annotation { "Feature Type Name" : "Feature", "Feature Type Description" : "" }
export const myFeature = defineFeature(function(context is Context, id is Id, definition is map)
    precondition{}
    {
        {
            assignVariable(context, id + "F0", {"name" : "Offset", "anyValue" : .2});
        }
        {
            assignVariable(context, id + "F1", {"name" : "WallThick", "anyValue" : 1.2});
        }
        {
            assignVariable(context, id + "F2", {"name" : "TileThick3", "anyValue" : 6});
        }
        {
            assignVariable(context, id + "F3", {"name" : "TileThick4", "anyValue" : 8});
        }
        {
            assignVariable(context, id + "F4", {"name" : "TileSide", "anyValue" : 20.2});
        }
        {
            var Q0;
            Q0=qCreatedBy(makeId("Front.planeOp"),FACE);
            var sketch = newSketch(context, id + "F5", { "sketchPlane" : qUnion([Q0])});
            skLineSegment(sketch, "E0.bottom", {"start": v(10.1, -10.1) * mm, "end": v(-10.1, -10.1) * mm});
            skLineSegment(sketch, "E0.top", {"start": v(10.1, 10.1) * mm, "end": v(-10.1, 10.1) * mm});
            skLineSegment(sketch, "E0.left", {"start": v(10.1, -10.1) * mm, "end": v(10.1, 10.1) * mm});
            skLineSegment(sketch, "E0.right", {"start": v(-10.1, -10.1) * mm, "end": v(-10.1, 10.1) * mm});
            skPoint(sketch, "E0.middle", {"position": v(0, 0) * mm});
            skSolve(sketch);
        }
        {
            var Q0;
            Q0 = qSketchRegion(id + "F5", true);
            extrude(context, id + "F6", {"entities" : qUnion([Q0]), "oppositeDirection" : true, "depth" : (getVariable(context, 'TileThick3')) * mm, "offsetDistance" : 25 * mm});
        }
        {
            var Q0;
            Q0=makeQuery(id+"F6.opExtrude","SWEPT_EDGE",EDGE,{"disambiguationData":[OSD([sQuery(id+"F5.wireOp",EDGE,"E0.top"),sQuery(id+"F5.wireOp",EDGE,"E0.left")])]});
            var Q1;
            Q1=makeQuery(id+"F6.opExtrude","SWEPT_EDGE",EDGE,{"disambiguationData":[OSD([sQuery(id+"F5.wireOp",EDGE,"E0.top"),sQuery(id+"F5.wireOp",EDGE,"E0.right")])]});
            var Q2;
            Q2=makeQuery(id+"F6.opExtrude","SWEPT_EDGE",EDGE,{"disambiguationData":[OSD([sQuery(id+"F5.wireOp",EDGE,"E0.bottom"),sQuery(id+"F5.wireOp",EDGE,"E0.right")])]});
            var Q3;
            Q3=makeQuery(id+"F6.opExtrude","SWEPT_EDGE",EDGE,{"disambiguationData":[OSD([sQuery(id+"F5.wireOp",EDGE,"E0.bottom"),sQuery(id+"F5.wireOp",EDGE,"E0.left")])]});
            fillet(context, id + "F7", {"entities" : qUnion([Q0, Q1, Q2, Q3]), "radius" : 1.5 * mm, "tangentPropagation" : true, "allowEdgeOverflow" : false});
        }
        {
            var Q0;
            Q0=makeQuery(id+"F6.opExtrude","SWEPT_FACE",FACE,{"disambiguationData":[OSD([sQuery(id+"F5.wireOp",EDGE,"E0.bottom")])]});
            cPlane(context, id + "F8", {"entities" : qUnion([Q0]), "cplaneType" : CPlaneType.OFFSET, "offset" : (getVariable(context, 'TileSide') - 8) * mm, "oppositeDirection" : true, "width" : 150 * mm, "height" : 150 * mm});
        }
        {
            var Q0;
            Q0=qCreatedBy(id+"F8.planeOp",FACE);
            var sketch = newSketch(context, id + "F9", { "sketchPlane" : qUnion([Q0])});
            skLineSegment(sketch, "E1.0", {"start": v(15, 0.2) * mm, "end": v(10.3, 0.2) * mm});
            skLineSegment(sketch, "E1.1", {"start": v(10.3, -6.2) * mm, "end": v(10.3, 0.2) * mm});
            skLineSegment(sketch, "E1.2", {"start": v(15, 0.2) * mm, "end": v(-2.2, 0.2) * mm});
            skLineSegment(sketch, "E1.3", {"start": v(10.3, -6.2) * mm, "end": v(15, -6.2) * mm});
            skLineSegment(sketch, "E1.4", {"start": v(-2.2, 0.2) * mm, "end": v(-10.3, 0.2) * mm});
            skLineSegment(sketch, "E1.5", {"start": v(-10.3, 0.2) * mm, "end": v(-10.3, -6.2) * mm});
            skLineSegment(sketch, "E1.6", {"start": v(-10.3, -6.2) * mm, "end": v(-2.2, -6.2) * mm});
            skLineSegment(sketch, "E1.7", {"start": v(15, -6.2) * mm, "end": v(-2.2, -6.2) * mm});
            skLineSegment(sketch, "E2.0", {"start": v(11.5, -7.4) * mm, "end": v(11.8, -7.4) * mm});
            skLineSegment(sketch, "E2.1", {"start": v(11.5, -7.4) * mm, "end": v(11.5, 1.4) * mm});
            skLineSegment(sketch, "E2.2", {"start": v(11.8, -7.4) * mm, "end": v(-2.2, -7.4) * mm});
            skLineSegment(sketch, "E2.3", {"start": v(15, 1.4) * mm, "end": v(11.5, 1.4) * mm});
            skLineSegment(sketch, "E2.4", {"start": v(-11.5, -7.4) * mm, "end": v(-2.2, -7.4) * mm});
            skLineSegment(sketch, "E2.5", {"start": v(-11.5, 1.4) * mm, "end": v(-11.5, -7.4) * mm});
            skLineSegment(sketch, "E2.6", {"start": v(-5.4, 1.4) * mm, "end": v(-11.5, 1.4) * mm});
            skLineSegment(sketch, "E2.7", {"start": v(15, 1.4) * mm, "end": v(-5.4, 1.4) * mm});
            skLineSegment(sketch, "E3.0.1.0", {"start": v(-11.5, -15) * mm, "end": v(-2.2, -15) * mm});
            skLineSegment(sketch, "E3.0.1.1", {"start": v(15, -6.2) * mm, "end": v(11.5, -6.2) * mm});
            skLineSegment(sketch, "E3.0.1.2", {"start": v(11.8, -15) * mm, "end": v(-2.2, -15) * mm});
            skLineSegment(sketch, "E3.0.1.3", {"start": v(11.5, -15) * mm, "end": v(11.5, -6.2) * mm});
            skLineSegment(sketch, "E3.0.1.4", {"start": v(11.5, -15) * mm, "end": v(11.8, -15) * mm});
            skLineSegment(sketch, "E3.0.1.5", {"start": v(15, -13.8) * mm, "end": v(-2.2, -13.8) * mm});
            skLineSegment(sketch, "E3.0.1.6", {"start": v(-10.3, -7.4) * mm, "end": v(-10.3, -13.8) * mm});
            skLineSegment(sketch, "E3.0.1.7", {"start": v(15, -7.4) * mm, "end": v(-2.2, -7.4) * mm});
            skLineSegment(sketch, "E3.0.1.8", {"start": v(10.3, -13.8) * mm, "end": v(10.3, -7.4) * mm});
            skLineSegment(sketch, "E3.0.1.9", {"start": v(15, -6.2) * mm, "end": v(-5.4, -6.2) * mm});
            skLineSegment(sketch, "E3.0.1.10", {"start": v(-5.4, -6.2) * mm, "end": v(-11.5, -6.2) * mm});
            skLineSegment(sketch, "E3.0.1.11", {"start": v(-11.5, -6.2) * mm, "end": v(-11.5, -15) * mm});
            skLineSegment(sketch, "E3.0.1.12", {"start": v(-10.3, -13.8) * mm, "end": v(-2.2, -13.8) * mm});
            skLineSegment(sketch, "E3.0.1.13", {"start": v(-2.2, -7.4) * mm, "end": v(-10.3, -7.4) * mm});
            skLineSegment(sketch, "E3.0.1.14", {"start": v(10.3, -13.8) * mm, "end": v(15, -13.8) * mm});
            skLineSegment(sketch, "E3.0.1.15", {"start": v(15, -7.4) * mm, "end": v(10.3, -7.4) * mm});
            skLineSegment(sketch, "E3.0.2.0", {"start": v(-11.5, -22.6) * mm, "end": v(-2.2, -22.6) * mm});
            skLineSegment(sketch, "E3.0.2.1", {"start": v(15, -13.8) * mm, "end": v(11.5, -13.8) * mm});
            skLineSegment(sketch, "E3.0.2.2", {"start": v(11.8, -22.6) * mm, "end": v(-2.2, -22.6) * mm});
            skLineSegment(sketch, "E3.0.2.3", {"start": v(11.5, -22.6) * mm, "end": v(11.5, -13.8) * mm});
            skLineSegment(sketch, "E3.0.2.4", {"start": v(11.5, -22.6) * mm, "end": v(11.8, -22.6) * mm});
            skLineSegment(sketch, "E3.0.2.5", {"start": v(15, -21.4) * mm, "end": v(-2.2, -21.4) * mm});
            skLineSegment(sketch, "E3.0.2.6", {"start": v(-10.3, -15) * mm, "end": v(-10.3, -21.4) * mm});
            skLineSegment(sketch, "E3.0.2.7", {"start": v(15, -15) * mm, "end": v(-2.2, -15) * mm});
            skLineSegment(sketch, "E3.0.2.8", {"start": v(10.3, -21.4) * mm, "end": v(10.3, -15) * mm});
            skLineSegment(sketch, "E3.0.2.9", {"start": v(15, -13.8) * mm, "end": v(-5.4, -13.8) * mm});
            skLineSegment(sketch, "E3.0.2.10", {"start": v(-5.4, -13.8) * mm, "end": v(-11.5, -13.8) * mm});
            skLineSegment(sketch, "E3.0.2.11", {"start": v(-11.5, -13.8) * mm, "end": v(-11.5, -22.6) * mm});
            skLineSegment(sketch, "E3.0.2.12", {"start": v(-10.3, -21.4) * mm, "end": v(-2.2, -21.4) * mm});
            skLineSegment(sketch, "E3.0.2.13", {"start": v(-2.2, -15) * mm, "end": v(-10.3, -15) * mm});
            skLineSegment(sketch, "E3.0.2.14", {"start": v(10.3, -21.4) * mm, "end": v(15, -21.4) * mm});
            skLineSegment(sketch, "E3.0.2.15", {"start": v(15, -15) * mm, "end": v(10.3, -15) * mm});
            skLineSegment(sketch, "E3.0.3.0", {"start": v(-11.5, -30.2) * mm, "end": v(-2.2, -30.2) * mm});
            skLineSegment(sketch, "E3.0.3.1", {"start": v(15, -21.4) * mm, "end": v(11.5, -21.4) * mm});
            skLineSegment(sketch, "E3.0.3.2", {"start": v(11.8, -30.2) * mm, "end": v(-2.2, -30.2) * mm});
            skLineSegment(sketch, "E3.0.3.3", {"start": v(11.5, -30.2) * mm, "end": v(11.5, -21.4) * mm});
            skLineSegment(sketch, "E3.0.3.4", {"start": v(11.5, -30.2) * mm, "end": v(11.8, -30.2) * mm});
            skLineSegment(sketch, "E3.0.3.5", {"start": v(15, -29) * mm, "end": v(-2.2, -29) * mm});
            skLineSegment(sketch, "E3.0.3.6", {"start": v(-10.3, -22.6) * mm, "end": v(-10.3, -29) * mm});
            skLineSegment(sketch, "E3.0.3.7", {"start": v(15, -22.6) * mm, "end": v(-2.2, -22.6) * mm});
            skLineSegment(sketch, "E3.0.3.8", {"start": v(10.3, -29) * mm, "end": v(10.3, -22.6) * mm});
            skLineSegment(sketch, "E3.0.3.9", {"start": v(15, -21.4) * mm, "end": v(-5.4, -21.4) * mm});
            skLineSegment(sketch, "E3.0.3.10", {"start": v(-5.4, -21.4) * mm, "end": v(-11.5, -21.4) * mm});
            skLineSegment(sketch, "E3.0.3.11", {"start": v(-11.5, -21.4) * mm, "end": v(-11.5, -30.2) * mm});
            skLineSegment(sketch, "E3.0.3.12", {"start": v(-10.3, -29) * mm, "end": v(-2.2, -29) * mm});
            skLineSegment(sketch, "E3.0.3.13", {"start": v(-2.2, -22.6) * mm, "end": v(-10.3, -22.6) * mm});
            skLineSegment(sketch, "E3.0.3.14", {"start": v(10.3, -29) * mm, "end": v(15, -29) * mm});
            skLineSegment(sketch, "E3.0.3.15", {"start": v(15, -22.6) * mm, "end": v(10.3, -22.6) * mm});
            skLineSegment(sketch, "E3.1.0.0", {"start": v(10.3, -7.4) * mm, "end": v(19.6, -7.4) * mm});
            skLineSegment(sketch, "E3.1.0.1", {"start": v(36.8, 1.4) * mm, "end": v(33.3, 1.4) * mm});
            skLineSegment(sketch, "E3.1.0.2", {"start": v(33.6, -7.4) * mm, "end": v(19.6, -7.4) * mm});
            skLineSegment(sketch, "E3.1.0.3", {"start": v(33.3, -7.4) * mm, "end": v(33.3, 1.4) * mm});
            skLineSegment(sketch, "E3.1.0.4", {"start": v(33.3, -7.4) * mm, "end": v(33.6, -7.4) * mm});
            skLineSegment(sketch, "E3.1.0.5", {"start": v(36.8, -6.2) * mm, "end": v(19.6, -6.2) * mm});
            skLineSegment(sketch, "E3.1.0.6", {"start": v(11.5, 0.2) * mm, "end": v(11.5, -6.2) * mm});
            skLineSegment(sketch, "E3.1.0.7", {"start": v(36.8, 0.2) * mm, "end": v(19.6, 0.2) * mm});
            skLineSegment(sketch, "E3.1.0.8", {"start": v(32.1, -6.2) * mm, "end": v(32.1, 0.2) * mm});
            skLineSegment(sketch, "E3.1.0.9", {"start": v(36.8, 1.4) * mm, "end": v(16.4, 1.4) * mm});
            skLineSegment(sketch, "E3.1.0.10", {"start": v(16.4, 1.4) * mm, "end": v(10.3, 1.4) * mm});
            skLineSegment(sketch, "E3.1.0.11", {"start": v(10.3, 1.4) * mm, "end": v(10.3, -7.4) * mm});
            skLineSegment(sketch, "E3.1.0.12", {"start": v(11.5, -6.2) * mm, "end": v(19.6, -6.2) * mm});
            skLineSegment(sketch, "E3.1.0.13", {"start": v(19.6, 0.2) * mm, "end": v(11.5, 0.2) * mm});
            skLineSegment(sketch, "E3.1.0.14", {"start": v(32.1, -6.2) * mm, "end": v(36.8, -6.2) * mm});
            skLineSegment(sketch, "E3.1.0.15", {"start": v(36.8, 0.2) * mm, "end": v(32.1, 0.2) * mm});
            skLineSegment(sketch, "E3.1.1.0", {"start": v(10.3, -15) * mm, "end": v(19.6, -15) * mm});
            skLineSegment(sketch, "E3.1.1.1", {"start": v(36.8, -6.2) * mm, "end": v(33.3, -6.2) * mm});
            skLineSegment(sketch, "E3.1.1.2", {"start": v(33.6, -15) * mm, "end": v(19.6, -15) * mm});
            skLineSegment(sketch, "E3.1.1.3", {"start": v(33.3, -15) * mm, "end": v(33.3, -6.2) * mm});
            skLineSegment(sketch, "E3.1.1.4", {"start": v(33.3, -15) * mm, "end": v(33.6, -15) * mm});
            skLineSegment(sketch, "E3.1.1.5", {"start": v(36.8, -13.8) * mm, "end": v(19.6, -13.8) * mm});
            skLineSegment(sketch, "E3.1.1.6", {"start": v(11.5, -7.4) * mm, "end": v(11.5, -13.8) * mm});
            skLineSegment(sketch, "E3.1.1.7", {"start": v(36.8, -7.4) * mm, "end": v(19.6, -7.4) * mm});
            skLineSegment(sketch, "E3.1.1.8", {"start": v(32.1, -13.8) * mm, "end": v(32.1, -7.4) * mm});
            skLineSegment(sketch, "E3.1.1.9", {"start": v(36.8, -6.2) * mm, "end": v(16.4, -6.2) * mm});
            skLineSegment(sketch, "E3.1.1.10", {"start": v(16.4, -6.2) * mm, "end": v(10.3, -6.2) * mm});
            skLineSegment(sketch, "E3.1.1.11", {"start": v(10.3, -6.2) * mm, "end": v(10.3, -15) * mm});
            skLineSegment(sketch, "E3.1.1.12", {"start": v(11.5, -13.8) * mm, "end": v(19.6, -13.8) * mm});
            skLineSegment(sketch, "E3.1.1.13", {"start": v(19.6, -7.4) * mm, "end": v(11.5, -7.4) * mm});
            skLineSegment(sketch, "E3.1.1.14", {"start": v(32.1, -13.8) * mm, "end": v(36.8, -13.8) * mm});
            skLineSegment(sketch, "E3.1.1.15", {"start": v(36.8, -7.4) * mm, "end": v(32.1, -7.4) * mm});
            skLineSegment(sketch, "E3.1.2.0", {"start": v(10.3, -22.6) * mm, "end": v(19.6, -22.6) * mm});
            skLineSegment(sketch, "E3.1.2.1", {"start": v(36.8, -13.8) * mm, "end": v(33.3, -13.8) * mm});
            skLineSegment(sketch, "E3.1.2.2", {"start": v(33.6, -22.6) * mm, "end": v(19.6, -22.6) * mm});
            skLineSegment(sketch, "E3.1.2.3", {"start": v(33.3, -22.6) * mm, "end": v(33.3, -13.8) * mm});
            skLineSegment(sketch, "E3.1.2.4", {"start": v(33.3, -22.6) * mm, "end": v(33.6, -22.6) * mm});
            skLineSegment(sketch, "E3.1.2.5", {"start": v(36.8, -21.4) * mm, "end": v(19.6, -21.4) * mm});
            skLineSegment(sketch, "E3.1.2.6", {"start": v(11.5, -15) * mm, "end": v(11.5, -21.4) * mm});
            skLineSegment(sketch, "E3.1.2.7", {"start": v(36.8, -15) * mm, "end": v(19.6, -15) * mm});
            skLineSegment(sketch, "E3.1.2.8", {"start": v(32.1, -21.4) * mm, "end": v(32.1, -15) * mm});
            skLineSegment(sketch, "E3.1.2.9", {"start": v(36.8, -13.8) * mm, "end": v(16.4, -13.8) * mm});
            skLineSegment(sketch, "E3.1.2.10", {"start": v(16.4, -13.8) * mm, "end": v(10.3, -13.8) * mm});
            skLineSegment(sketch, "E3.1.2.11", {"start": v(10.3, -13.8) * mm, "end": v(10.3, -22.6) * mm});
            skLineSegment(sketch, "E3.1.2.12", {"start": v(11.5, -21.4) * mm, "end": v(19.6, -21.4) * mm});
            skLineSegment(sketch, "E3.1.2.13", {"start": v(19.6, -15) * mm, "end": v(11.5, -15) * mm});
            skLineSegment(sketch, "E3.1.2.14", {"start": v(32.1, -21.4) * mm, "end": v(36.8, -21.4) * mm});
            skLineSegment(sketch, "E3.1.2.15", {"start": v(36.8, -15) * mm, "end": v(32.1, -15) * mm});
            skLineSegment(sketch, "E3.1.3.0", {"start": v(10.3, -30.2) * mm, "end": v(19.6, -30.2) * mm});
            skLineSegment(sketch, "E3.1.3.1", {"start": v(36.8, -21.4) * mm, "end": v(33.3, -21.4) * mm});
            skLineSegment(sketch, "E3.1.3.2", {"start": v(33.6, -30.2) * mm, "end": v(19.6, -30.2) * mm});
            skLineSegment(sketch, "E3.1.3.3", {"start": v(33.3, -30.2) * mm, "end": v(33.3, -21.4) * mm});
            skLineSegment(sketch, "E3.1.3.4", {"start": v(33.3, -30.2) * mm, "end": v(33.6, -30.2) * mm});
            skLineSegment(sketch, "E3.1.3.5", {"start": v(36.8, -29) * mm, "end": v(19.6, -29) * mm});
            skLineSegment(sketch, "E3.1.3.6", {"start": v(11.5, -22.6) * mm, "end": v(11.5, -29) * mm});
            skLineSegment(sketch, "E3.1.3.7", {"start": v(36.8, -22.6) * mm, "end": v(19.6, -22.6) * mm});
            skLineSegment(sketch, "E3.1.3.8", {"start": v(32.1, -29) * mm, "end": v(32.1, -22.6) * mm});
            skLineSegment(sketch, "E3.1.3.9", {"start": v(36.8, -21.4) * mm, "end": v(16.4, -21.4) * mm});
            skLineSegment(sketch, "E3.1.3.10", {"start": v(16.4, -21.4) * mm, "end": v(10.3, -21.4) * mm});
            skLineSegment(sketch, "E3.1.3.11", {"start": v(10.3, -21.4) * mm, "end": v(10.3, -30.2) * mm});
            skLineSegment(sketch, "E3.1.3.12", {"start": v(11.5, -29) * mm, "end": v(19.6, -29) * mm});
            skLineSegment(sketch, "E3.1.3.13", {"start": v(19.6, -22.6) * mm, "end": v(11.5, -22.6) * mm});
            skLineSegment(sketch, "E3.1.3.14", {"start": v(32.1, -29) * mm, "end": v(36.8, -29) * mm});
            skLineSegment(sketch, "E3.1.3.15", {"start": v(36.8, -22.6) * mm, "end": v(32.1, -22.6) * mm});
            skLineSegment(sketch, "E3.2.0.0", {"start": v(32.1, -7.4) * mm, "end": v(41.4, -7.4) * mm});
            skLineSegment(sketch, "E3.2.0.1", {"start": v(58.6, 1.4) * mm, "end": v(55.1, 1.4) * mm});
            skLineSegment(sketch, "E3.2.0.2", {"start": v(55.4, -7.4) * mm, "end": v(41.4, -7.4) * mm});
            skLineSegment(sketch, "E3.2.0.3", {"start": v(55.1, -7.4) * mm, "end": v(55.1, 1.4) * mm});
            skLineSegment(sketch, "E3.2.0.4", {"start": v(55.1, -7.4) * mm, "end": v(55.4, -7.4) * mm});
            skLineSegment(sketch, "E3.2.0.5", {"start": v(58.6, -6.2) * mm, "end": v(41.4, -6.2) * mm});
            skLineSegment(sketch, "E3.2.0.6", {"start": v(33.3, 0.2) * mm, "end": v(33.3, -6.2) * mm});
            skLineSegment(sketch, "E3.2.0.7", {"start": v(58.6, 0.2) * mm, "end": v(41.4, 0.2) * mm});
            skLineSegment(sketch, "E3.2.0.8", {"start": v(53.9, -6.2) * mm, "end": v(53.9, 0.2) * mm});
            skLineSegment(sketch, "E3.2.0.9", {"start": v(58.6, 1.4) * mm, "end": v(38.2, 1.4) * mm});
            skLineSegment(sketch, "E3.2.0.10", {"start": v(38.2, 1.4) * mm, "end": v(32.1, 1.4) * mm});
            skLineSegment(sketch, "E3.2.0.11", {"start": v(32.1, 1.4) * mm, "end": v(32.1, -7.4) * mm});
            skLineSegment(sketch, "E3.2.0.12", {"start": v(33.3, -6.2) * mm, "end": v(41.4, -6.2) * mm});
            skLineSegment(sketch, "E3.2.0.13", {"start": v(41.4, 0.2) * mm, "end": v(33.3, 0.2) * mm});
            skLineSegment(sketch, "E3.2.0.14", {"start": v(53.9, -6.2) * mm, "end": v(58.6, -6.2) * mm});
            skLineSegment(sketch, "E3.2.0.15", {"start": v(58.6, 0.2) * mm, "end": v(53.9, 0.2) * mm});
            skLineSegment(sketch, "E3.2.1.0", {"start": v(32.1, -15) * mm, "end": v(41.4, -15) * mm});
            skLineSegment(sketch, "E3.2.1.1", {"start": v(58.6, -6.2) * mm, "end": v(55.1, -6.2) * mm});
            skLineSegment(sketch, "E3.2.1.2", {"start": v(55.4, -15) * mm, "end": v(41.4, -15) * mm});
            skLineSegment(sketch, "E3.2.1.3", {"start": v(55.1, -15) * mm, "end": v(55.1, -6.2) * mm});
            skLineSegment(sketch, "E3.2.1.4", {"start": v(55.1, -15) * mm, "end": v(55.4, -15) * mm});
            skLineSegment(sketch, "E3.2.1.5", {"start": v(58.6, -13.8) * mm, "end": v(41.4, -13.8) * mm});
            skLineSegment(sketch, "E3.2.1.6", {"start": v(33.3, -7.4) * mm, "end": v(33.3, -13.8) * mm});
            skLineSegment(sketch, "E3.2.1.7", {"start": v(58.6, -7.4) * mm, "end": v(41.4, -7.4) * mm});
            skLineSegment(sketch, "E3.2.1.8", {"start": v(53.9, -13.8) * mm, "end": v(53.9, -7.4) * mm});
            skLineSegment(sketch, "E3.2.1.9", {"start": v(58.6, -6.2) * mm, "end": v(38.2, -6.2) * mm});
            skLineSegment(sketch, "E3.2.1.10", {"start": v(38.2, -6.2) * mm, "end": v(32.1, -6.2) * mm});
            skLineSegment(sketch, "E3.2.1.11", {"start": v(32.1, -6.2) * mm, "end": v(32.1, -15) * mm});
            skLineSegment(sketch, "E3.2.1.12", {"start": v(33.3, -13.8) * mm, "end": v(41.4, -13.8) * mm});
            skLineSegment(sketch, "E3.2.1.13", {"start": v(41.4, -7.4) * mm, "end": v(33.3, -7.4) * mm});
            skLineSegment(sketch, "E3.2.1.14", {"start": v(53.9, -13.8) * mm, "end": v(58.6, -13.8) * mm});
            skLineSegment(sketch, "E3.2.1.15", {"start": v(58.6, -7.4) * mm, "end": v(53.9, -7.4) * mm});
            skLineSegment(sketch, "E3.2.2.0", {"start": v(32.1, -22.6) * mm, "end": v(41.4, -22.6) * mm});
            skLineSegment(sketch, "E3.2.2.1", {"start": v(58.6, -13.8) * mm, "end": v(55.1, -13.8) * mm});
            skLineSegment(sketch, "E3.2.2.2", {"start": v(55.4, -22.6) * mm, "end": v(41.4, -22.6) * mm});
            skLineSegment(sketch, "E3.2.2.3", {"start": v(55.1, -22.6) * mm, "end": v(55.1, -13.8) * mm});
            skLineSegment(sketch, "E3.2.2.4", {"start": v(55.1, -22.6) * mm, "end": v(55.4, -22.6) * mm});
            skLineSegment(sketch, "E3.2.2.5", {"start": v(58.6, -21.4) * mm, "end": v(41.4, -21.4) * mm});
            skLineSegment(sketch, "E3.2.2.6", {"start": v(33.3, -15) * mm, "end": v(33.3, -21.4) * mm});
            skLineSegment(sketch, "E3.2.2.7", {"start": v(58.6, -15) * mm, "end": v(41.4, -15) * mm});
            skLineSegment(sketch, "E3.2.2.8", {"start": v(53.9, -21.4) * mm, "end": v(53.9, -15) * mm});
            skLineSegment(sketch, "E3.2.2.9", {"start": v(58.6, -13.8) * mm, "end": v(38.2, -13.8) * mm});
            skLineSegment(sketch, "E3.2.2.10", {"start": v(38.2, -13.8) * mm, "end": v(32.1, -13.8) * mm});
            skLineSegment(sketch, "E3.2.2.11", {"start": v(32.1, -13.8) * mm, "end": v(32.1, -22.6) * mm});
            skLineSegment(sketch, "E3.2.2.12", {"start": v(33.3, -21.4) * mm, "end": v(41.4, -21.4) * mm});
            skLineSegment(sketch, "E3.2.2.13", {"start": v(41.4, -15) * mm, "end": v(33.3, -15) * mm});
            skLineSegment(sketch, "E3.2.2.14", {"start": v(53.9, -21.4) * mm, "end": v(58.6, -21.4) * mm});
            skLineSegment(sketch, "E3.2.2.15", {"start": v(58.6, -15) * mm, "end": v(53.9, -15) * mm});
            skLineSegment(sketch, "E3.2.3.0", {"start": v(32.1, -30.2) * mm, "end": v(41.4, -30.2) * mm});
            skLineSegment(sketch, "E3.2.3.1", {"start": v(58.6, -21.4) * mm, "end": v(55.1, -21.4) * mm});
            skLineSegment(sketch, "E3.2.3.2", {"start": v(55.4, -30.2) * mm, "end": v(41.4, -30.2) * mm});
            skLineSegment(sketch, "E3.2.3.3", {"start": v(55.1, -30.2) * mm, "end": v(55.1, -21.4) * mm});
            skLineSegment(sketch, "E3.2.3.4", {"start": v(55.1, -30.2) * mm, "end": v(55.4, -30.2) * mm});
            skLineSegment(sketch, "E3.2.3.5", {"start": v(55.1, -29) * mm, "end": v(41.4, -29) * mm});
            skLineSegment(sketch, "E3.2.3.6", {"start": v(33.3, -22.6) * mm, "end": v(33.3, -29) * mm});
            skLineSegment(sketch, "E3.2.3.7", {"start": v(58.6, -22.6) * mm, "end": v(41.4, -22.6) * mm});
            skLineSegment(sketch, "E3.2.3.8", {"start": v(53.9, -29) * mm, "end": v(53.9, -22.6) * mm});
            skLineSegment(sketch, "E3.2.3.9", {"start": v(58.6, -21.4) * mm, "end": v(38.2, -21.4) * mm});
            skLineSegment(sketch, "E3.2.3.10", {"start": v(38.2, -21.4) * mm, "end": v(32.1, -21.4) * mm});
            skLineSegment(sketch, "E3.2.3.11", {"start": v(32.1, -21.4) * mm, "end": v(32.1, -30.2) * mm});
            skLineSegment(sketch, "E3.2.3.12", {"start": v(33.3, -29) * mm, "end": v(41.4, -29) * mm});
            skLineSegment(sketch, "E3.2.3.13", {"start": v(41.4, -22.6) * mm, "end": v(33.3, -22.6) * mm});
            skLineSegment(sketch, "E3.2.3.14", {"start": v(53.9, -29) * mm, "end": v(58.6, -29) * mm});
            skLineSegment(sketch, "E3.2.3.15", {"start": v(58.6, -22.6) * mm, "end": v(53.9, -22.6) * mm});
            skLineSegment(sketch, "E3.direction1", {"start": v(-11.5, -7.4) * mm, "end": v(10.3, -7.4) * mm, "construction": true});
            skLineSegment(sketch, "E3.direction2", {"start": v(-11.5, -7.4) * mm, "end": v(-11.5, -15) * mm, "construction": true});
            skSolve(sketch);
        }
        {
            var Q0;
            Q0=makeQuery(id+"F6.opExtrude","SWEPT_FACE",FACE,{"disambiguationData":[OSD([sQuery(id+"F5.wireOp",EDGE,"E0.bottom")])]});
            cPlane(context, id + "F10", {"entities" : qUnion([Q0]), "cplaneType" : CPlaneType.OFFSET, "offset" : (getVariable(context, 'WallThick')) * mm, "width" : 150 * mm, "height" : 150 * mm});
        }
        {
            var Q0;
            Q0=qCreatedBy(id+"F10.planeOp",FACE);
            var sketch = newSketch(context, id + "F11", { "sketchPlane" : qUnion([Q0])});
            skLineSegment(sketch, "E4.bottom", {"start": v(-11.5, 1.4) * mm, "end": v(55.1, 1.4) * mm});
            skLineSegment(sketch, "E4.top", {"start": v(-11.5, -30.2) * mm, "end": v(55.1, -30.2) * mm});
            skLineSegment(sketch, "E4.left", {"start": v(-11.5, 1.4) * mm, "end": v(-11.5, -30.2) * mm});
            skLineSegment(sketch, "E4.right", {"start": v(55.1, 1.4) * mm, "end": v(55.1, -30.2) * mm});
            skSolve(sketch);
        }
        {
            var Q0;
            Q0=makeQuery(id+"F11.imprint","IMPRINT",FACE,{"disambiguationData":[TD([[makeQuery(id+"F11.imprint","IMPRINT",EDGE,{"derivedFrom":sQuery(id+"F11.wireOp",EDGE,"E4.bottom")}),-1.0]])]});
            var Q1;
            Q1=qCreatedBy(id+"F8.planeOp",FACE);
            extrude(context, id + "F12", {"entities" : qUnion([Q0]), "endBound" : BoundingType.UP_TO_SURFACE, "oppositeDirection" : true, "depth" : 25 * mm, "endBoundEntityFace" : qUnion([Q1]), "offsetDistance" : 25 * mm});
        }
        {
            var Q0;
            Q0=makeQuery(id+"F12.opExtrude","SWEPT_FACE",FACE,{"disambiguationData":[OSD([sQuery(id+"F11.wireOp",EDGE,"E4.top")])]});
            cPlane(context, id + "F13", {"entities" : qUnion([Q0]), "cplaneType" : CPlaneType.OFFSET, "offset" : (getVariable(context, 'Offset')) * mm, "width" : 150 * mm, "height" : 150 * mm});
        }
        {
            var Q0;
            Q0=qCreatedBy(id+"F13.planeOp",FACE);
            var sketch = newSketch(context, id + "F14", { "sketchPlane" : qUnion([Q0])});
            skPoint(sketch, "E5.middle", {"position": v(0, 0) * mm});
            skLineSegment(sketch, "E6.bottom", {"start": v(10.1, -10.1) * mm, "end": v(-10.1, -10.1) * mm});
            skLineSegment(sketch, "E6.top", {"start": v(10.1, 10.1) * mm, "end": v(-10.1, 10.1) * mm});
            skLineSegment(sketch, "E6.left", {"start": v(10.1, -10.1) * mm, "end": v(10.1, 10.1) * mm});
            skLineSegment(sketch, "E6.right", {"start": v(-10.1, -10.1) * mm, "end": v(-10.1, 10.1) * mm});
            skSolve(sketch);
        }
        {
            var Q0;
            Q0=makeQuery(id+"F14.imprint","IMPRINT",FACE,{"disambiguationData":[TD([[makeQuery(id+"F14.imprint","IMPRINT",EDGE,{"derivedFrom":sQuery(id+"F14.wireOp",EDGE,"E6.bottom")}),-1.0]])]});
            extrude(context, id + "F15", {"entities" : qUnion([Q0]), "depth" : (getVariable(context, 'TileThick4')) * mm, "offsetDistance" : 25 * mm});
        }
        {
            var Q0;
            Q0=makeQuery(id+"F15.opExtrude","SWEPT_EDGE",EDGE,{"disambiguationData":[OSD([sQuery(id+"F14.wireOp",EDGE,"E6.top"),sQuery(id+"F14.wireOp",EDGE,"E6.right")])]});
            var Q1;
            Q1=makeQuery(id+"F15.opExtrude","SWEPT_EDGE",EDGE,{"disambiguationData":[OSD([sQuery(id+"F14.wireOp",EDGE,"E6.top"),sQuery(id+"F14.wireOp",EDGE,"E6.left")])]});
            var Q2;
            Q2=makeQuery(id+"F15.opExtrude","SWEPT_EDGE",EDGE,{"disambiguationData":[OSD([sQuery(id+"F14.wireOp",EDGE,"E6.bottom"),sQuery(id+"F14.wireOp",EDGE,"E6.left")])]});
            var Q3;
            Q3=makeQuery(id+"F15.opExtrude","SWEPT_EDGE",EDGE,{"disambiguationData":[OSD([sQuery(id+"F14.wireOp",EDGE,"E6.bottom"),sQuery(id+"F14.wireOp",EDGE,"E6.right")])]});
            fillet(context, id + "F16", {"entities" : qUnion([Q0, Q1, Q2, Q3]), "radius" : 1.5 * mm, "tangentPropagation" : true, "allowEdgeOverflow" : false});
        }
        {
            var Q0;
            Q0=qCreatedBy(id+"F8.planeOp",FACE);
            var sketch = newSketch(context, id + "F17", { "sketchPlane" : qUnion([Q0])});
            skLineSegment(sketch, "E7.0", {"start": v(-10.3, -38.6) * mm, "end": v(-8.6, -38.6) * mm});
            skLineSegment(sketch, "E7.1", {"start": v(-10.3, -30.2) * mm, "end": v(-10.3, -38.6) * mm});
            skLineSegment(sketch, "E7.2", {"start": v(-8.6, -38.6) * mm, "end": v(8.6, -38.6) * mm});
            skLineSegment(sketch, "E7.3", {"start": v(-8.6, -30.2) * mm, "end": v(-10.3, -30.2) * mm});
            skLineSegment(sketch, "E7.4", {"start": v(8.6, -38.6) * mm, "end": v(10.3, -38.6) * mm});
            skLineSegment(sketch, "E7.5", {"start": v(10.3, -38.6) * mm, "end": v(10.3, -30.2) * mm});
            skLineSegment(sketch, "E7.6", {"start": v(10.3, -30.2) * mm, "end": v(8.6, -30.2) * mm});
            skLineSegment(sketch, "E7.7", {"start": v(-8.6, -30.2) * mm, "end": v(8.6, -30.2) * mm});
            skLineSegment(sketch, "E8.0", {"start": v(-11.5, -39.8) * mm, "end": v(-8.6, -39.8) * mm});
            skLineSegment(sketch, "E8.1", {"start": v(-11.5, -29) * mm, "end": v(-11.5, -39.8) * mm});
            skLineSegment(sketch, "E8.2", {"start": v(-8.6, -39.8) * mm, "end": v(8.6, -39.8) * mm});
            skLineSegment(sketch, "E8.3", {"start": v(-8.6, -29) * mm, "end": v(-11.5, -29) * mm});
            skLineSegment(sketch, "E8.4", {"start": v(8.6, -39.8) * mm, "end": v(11.5, -39.8) * mm});
            skLineSegment(sketch, "E8.5", {"start": v(11.5, -39.8) * mm, "end": v(11.5, -29) * mm});
            skLineSegment(sketch, "E8.6", {"start": v(11.5, -29) * mm, "end": v(8.6, -29) * mm});
            skLineSegment(sketch, "E8.7", {"start": v(-8.6, -29) * mm, "end": v(8.6, -29) * mm});
            skLineSegment(sketch, "E9.0.1.0", {"start": v(11.5, -38.6) * mm, "end": v(8.6, -38.6) * mm});
            skLineSegment(sketch, "E9.0.1.1", {"start": v(-8.6, -38.6) * mm, "end": v(-11.5, -38.6) * mm});
            skLineSegment(sketch, "E9.0.1.2", {"start": v(8.6, -48.2) * mm, "end": v(10.3, -48.2) * mm});
            skLineSegment(sketch, "E9.0.1.3", {"start": v(11.5, -49.4) * mm, "end": v(11.5, -38.6) * mm});
            skLineSegment(sketch, "E9.0.1.4", {"start": v(-10.3, -39.8) * mm, "end": v(-10.3, -48.2) * mm});
            skLineSegment(sketch, "E9.0.1.6", {"start": v(-8.6, -49.4) * mm, "end": v(8.6, -49.4) * mm});
            skLineSegment(sketch, "E9.0.1.7", {"start": v(8.6, -49.4) * mm, "end": v(11.5, -49.4) * mm});
            skLineSegment(sketch, "E9.0.1.8", {"start": v(-11.5, -38.6) * mm, "end": v(-11.5, -49.4) * mm});
            skLineSegment(sketch, "E9.0.1.9", {"start": v(-8.6, -48.2) * mm, "end": v(8.6, -48.2) * mm});
            skLineSegment(sketch, "E9.0.1.10", {"start": v(-11.5, -49.4) * mm, "end": v(-8.6, -49.4) * mm});
            skLineSegment(sketch, "E9.0.1.11", {"start": v(10.3, -39.8) * mm, "end": v(8.6, -39.8) * mm});
            skLineSegment(sketch, "E9.0.1.12", {"start": v(10.3, -48.2) * mm, "end": v(10.3, -39.8) * mm});
            skLineSegment(sketch, "E9.0.1.14", {"start": v(-10.3, -48.2) * mm, "end": v(-8.6, -48.2) * mm});
            skLineSegment(sketch, "E9.0.1.15", {"start": v(-8.6, -39.8) * mm, "end": v(-10.3, -39.8) * mm});
            skLineSegment(sketch, "E9.1.0.0", {"start": v(33.3, -29) * mm, "end": v(30.4, -29) * mm});
            skLineSegment(sketch, "E9.1.0.1", {"start": v(13.2, -29) * mm, "end": v(10.3, -29) * mm});
            skLineSegment(sketch, "E9.1.0.2", {"start": v(30.4, -38.6) * mm, "end": v(32.1, -38.6) * mm});
            skLineSegment(sketch, "E9.1.0.3", {"start": v(33.3, -39.8) * mm, "end": v(33.3, -29) * mm});
            skLineSegment(sketch, "E9.1.0.4", {"start": v(11.5, -30.2) * mm, "end": v(11.5, -38.6) * mm});
            skLineSegment(sketch, "E9.1.0.5", {"start": v(13.2, -29) * mm, "end": v(30.4, -29) * mm});
            skLineSegment(sketch, "E9.1.0.6", {"start": v(13.2, -39.8) * mm, "end": v(30.4, -39.8) * mm});
            skLineSegment(sketch, "E9.1.0.7", {"start": v(30.4, -39.8) * mm, "end": v(33.3, -39.8) * mm});
            skLineSegment(sketch, "E9.1.0.8", {"start": v(10.3, -29) * mm, "end": v(10.3, -39.8) * mm});
            skLineSegment(sketch, "E9.1.0.9", {"start": v(13.2, -38.6) * mm, "end": v(30.4, -38.6) * mm});
            skLineSegment(sketch, "E9.1.0.10", {"start": v(10.3, -39.8) * mm, "end": v(13.2, -39.8) * mm});
            skLineSegment(sketch, "E9.1.0.11", {"start": v(32.1, -30.2) * mm, "end": v(30.4, -30.2) * mm});
            skLineSegment(sketch, "E9.1.0.12", {"start": v(32.1, -38.6) * mm, "end": v(32.1, -30.2) * mm});
            skLineSegment(sketch, "E9.1.0.13", {"start": v(13.2, -30.2) * mm, "end": v(30.4, -30.2) * mm});
            skLineSegment(sketch, "E9.1.0.14", {"start": v(11.5, -38.6) * mm, "end": v(13.2, -38.6) * mm});
            skLineSegment(sketch, "E9.1.0.15", {"start": v(13.2, -30.2) * mm, "end": v(11.5, -30.2) * mm});
            skLineSegment(sketch, "E9.1.1.0", {"start": v(33.3, -38.6) * mm, "end": v(30.4, -38.6) * mm});
            skLineSegment(sketch, "E9.1.1.1", {"start": v(13.2, -38.6) * mm, "end": v(10.3, -38.6) * mm});
            skLineSegment(sketch, "E9.1.1.2", {"start": v(30.4, -48.2) * mm, "end": v(32.1, -48.2) * mm});
            skLineSegment(sketch, "E9.1.1.3", {"start": v(33.3, -49.4) * mm, "end": v(33.3, -38.6) * mm});
            skLineSegment(sketch, "E9.1.1.4", {"start": v(11.5, -39.8) * mm, "end": v(11.5, -48.2) * mm});
            skLineSegment(sketch, "E9.1.1.5", {"start": v(13.2, -38.6) * mm, "end": v(30.4, -38.6) * mm});
            skLineSegment(sketch, "E9.1.1.6", {"start": v(13.2, -49.4) * mm, "end": v(30.4, -49.4) * mm});
            skLineSegment(sketch, "E9.1.1.7", {"start": v(30.4, -49.4) * mm, "end": v(33.3, -49.4) * mm});
            skLineSegment(sketch, "E9.1.1.8", {"start": v(10.3, -38.6) * mm, "end": v(10.3, -49.4) * mm});
            skLineSegment(sketch, "E9.1.1.9", {"start": v(13.2, -48.2) * mm, "end": v(30.4, -48.2) * mm});
            skLineSegment(sketch, "E9.1.1.10", {"start": v(10.3, -49.4) * mm, "end": v(13.2, -49.4) * mm});
            skLineSegment(sketch, "E9.1.1.11", {"start": v(32.1, -39.8) * mm, "end": v(30.4, -39.8) * mm});
            skLineSegment(sketch, "E9.1.1.12", {"start": v(32.1, -48.2) * mm, "end": v(32.1, -39.8) * mm});
            skLineSegment(sketch, "E9.1.1.13", {"start": v(13.2, -39.8) * mm, "end": v(30.4, -39.8) * mm});
            skLineSegment(sketch, "E9.1.1.14", {"start": v(11.5, -48.2) * mm, "end": v(13.2, -48.2) * mm});
            skLineSegment(sketch, "E9.1.1.15", {"start": v(13.2, -39.8) * mm, "end": v(11.5, -39.8) * mm});
            skLineSegment(sketch, "E9.2.0.0", {"start": v(55.1, -29) * mm, "end": v(52.2, -29) * mm});
            skLineSegment(sketch, "E9.2.0.1", {"start": v(35, -29) * mm, "end": v(32.1, -29) * mm});
            skLineSegment(sketch, "E9.2.0.2", {"start": v(52.2, -38.6) * mm, "end": v(53.9, -38.6) * mm});
            skLineSegment(sketch, "E9.2.0.3", {"start": v(55.1, -39.8) * mm, "end": v(55.1, -29) * mm});
            skLineSegment(sketch, "E9.2.0.4", {"start": v(33.3, -30.2) * mm, "end": v(33.3, -38.6) * mm});
            skLineSegment(sketch, "E9.2.0.5", {"start": v(35, -29) * mm, "end": v(52.2, -29) * mm});
            skLineSegment(sketch, "E9.2.0.6", {"start": v(35, -39.8) * mm, "end": v(52.2, -39.8) * mm});
            skLineSegment(sketch, "E9.2.0.7", {"start": v(52.2, -39.8) * mm, "end": v(55.1, -39.8) * mm});
            skLineSegment(sketch, "E9.2.0.8", {"start": v(32.1, -29) * mm, "end": v(32.1, -39.8) * mm});
            skLineSegment(sketch, "E9.2.0.9", {"start": v(35, -38.6) * mm, "end": v(52.2, -38.6) * mm});
            skLineSegment(sketch, "E9.2.0.10", {"start": v(32.1, -39.8) * mm, "end": v(35, -39.8) * mm});
            skLineSegment(sketch, "E9.2.0.11", {"start": v(53.9, -30.2) * mm, "end": v(52.2, -30.2) * mm});
            skLineSegment(sketch, "E9.2.0.12", {"start": v(53.9, -38.6) * mm, "end": v(53.9, -30.2) * mm});
            skLineSegment(sketch, "E9.2.0.13", {"start": v(35, -30.2) * mm, "end": v(52.2, -30.2) * mm});
            skLineSegment(sketch, "E9.2.0.14", {"start": v(33.3, -38.6) * mm, "end": v(35, -38.6) * mm});
            skLineSegment(sketch, "E9.2.0.15", {"start": v(35, -30.2) * mm, "end": v(33.3, -30.2) * mm});
            skLineSegment(sketch, "E9.2.1.0", {"start": v(55.1, -38.6) * mm, "end": v(52.2, -38.6) * mm});
            skLineSegment(sketch, "E9.2.1.1", {"start": v(35, -38.6) * mm, "end": v(32.1, -38.6) * mm});
            skLineSegment(sketch, "E9.2.1.2", {"start": v(52.2, -48.2) * mm, "end": v(53.9, -48.2) * mm});
            skLineSegment(sketch, "E9.2.1.3", {"start": v(55.1, -49.4) * mm, "end": v(55.1, -38.6) * mm});
            skLineSegment(sketch, "E9.2.1.4", {"start": v(33.3, -39.8) * mm, "end": v(33.3, -48.2) * mm});
            skLineSegment(sketch, "E9.2.1.5", {"start": v(35, -38.6) * mm, "end": v(52.2, -38.6) * mm});
            skLineSegment(sketch, "E9.2.1.6", {"start": v(35, -49.4) * mm, "end": v(52.2, -49.4) * mm});
            skLineSegment(sketch, "E9.2.1.7", {"start": v(52.2, -49.4) * mm, "end": v(55.1, -49.4) * mm});
            skLineSegment(sketch, "E9.2.1.8", {"start": v(32.1, -38.6) * mm, "end": v(32.1, -49.4) * mm});
            skLineSegment(sketch, "E9.2.1.9", {"start": v(35, -48.2) * mm, "end": v(52.2, -48.2) * mm});
            skLineSegment(sketch, "E9.2.1.10", {"start": v(32.1, -49.4) * mm, "end": v(35, -49.4) * mm});
            skLineSegment(sketch, "E9.2.1.11", {"start": v(53.9, -39.8) * mm, "end": v(52.2, -39.8) * mm});
            skLineSegment(sketch, "E9.2.1.12", {"start": v(53.9, -48.2) * mm, "end": v(53.9, -39.8) * mm});
            skLineSegment(sketch, "E9.2.1.13", {"start": v(35, -39.8) * mm, "end": v(52.2, -39.8) * mm});
            skLineSegment(sketch, "E9.2.1.14", {"start": v(33.3, -48.2) * mm, "end": v(35, -48.2) * mm});
            skLineSegment(sketch, "E9.2.1.15", {"start": v(35, -39.8) * mm, "end": v(33.3, -39.8) * mm});
            skLineSegment(sketch, "E9.direction1", {"start": v(-11.5, -39.8) * mm, "end": v(10.3, -39.8) * mm, "construction": true});
            skLineSegment(sketch, "E9.direction2", {"start": v(-11.5, -39.8) * mm, "end": v(-11.5, -49.4) * mm, "construction": true});
            skSolve(sketch);
        }
        {
            var Q0;
            Q0=qCreatedBy(id+"F10.planeOp",FACE);
            var sketch = newSketch(context, id + "F18", { "sketchPlane" : qUnion([Q0])});
            skLineSegment(sketch, "E10.bottom", {"start": v(-11.5, -49.4) * mm, "end": v(55.1, -49.4) * mm});
            skLineSegment(sketch, "E10.top", {"start": v(-11.5, -29) * mm, "end": v(55.1, -29) * mm});
            skLineSegment(sketch, "E10.left", {"start": v(-11.5, -49.4) * mm, "end": v(-11.5, -29) * mm});
            skLineSegment(sketch, "E10.right", {"start": v(55.1, -49.4) * mm, "end": v(55.1, -29) * mm});
            skSolve(sketch);
        }
        {
            var Q0;
            Q0=makeQuery(id+"F18.imprint","IMPRINT",FACE,{"disambiguationData":[TD([[makeQuery(id+"F18.imprint","IMPRINT",EDGE,{"derivedFrom":sQuery(id+"F18.wireOp",EDGE,"E10.bottom")}),1.0]])]});
            var Q1;
            Q1=qCreatedBy(id+"F8.planeOp",FACE);
            extrude(context, id + "F19", {"entities" : qUnion([Q0]), "operationType" : NewBodyOperationType.ADD, "endBound" : BoundingType.UP_TO_SURFACE, "oppositeDirection" : true, "depth" : 25 * mm, "endBoundEntityFace" : qUnion([Q1]), "offsetDistance" : 25 * mm});
        }
        {
            var Q0;
            {var subQ3=sQuery(id+"F9.wireOp",EDGE,"E3.0.1.6");Q0=makeQuery(id+"F9.imprint","IMPRINT",FACE,{"disambiguationData":[TD([[makeQuery(id+"F9.imprint","IMPRINT",EDGE,{"derivedFrom":subQ3}),1.0]])]});}
            var Q1;
            {var subQ1=sQuery(id+"F9.wireOp",EDGE,"E1.4");Q1=makeQuery(id+"F9.imprint","IMPRINT",FACE,{"disambiguationData":[TD([[makeQuery(id+"F9.imprint","IMPRINT",EDGE,{"derivedFrom":subQ1}),1.0]])]});}
            var Q2;
            {var subQ2=sQuery(id+"F9.wireOp",EDGE,"E3.0.2.6");Q2=makeQuery(id+"F9.imprint","IMPRINT",FACE,{"disambiguationData":[TD([[makeQuery(id+"F9.imprint","IMPRINT",EDGE,{"derivedFrom":subQ2}),1.0]])]});}
            var Q3;
            {var subQ1=sQuery(id+"F9.wireOp",EDGE,"E3.0.3.5");Q3=makeQuery(id+"F9.imprint","IMPRINT",FACE,{"disambiguationData":[TD([[makeQuery(id+"F9.imprint","IMPRINT",EDGE,{"derivedFrom":subQ1}),-1.0]])]});}
            var Q4;
            {var subQ8=sQuery(id+"F9.wireOp",EDGE,"E3.1.3.5");Q4=makeQuery(id+"F9.imprint","IMPRINT",FACE,{"disambiguationData":[TD([[makeQuery(id+"F9.imprint","IMPRINT",EDGE,{"derivedFrom":subQ8}),-1.0]])]});}
            var Q5;
            {var subQ8=sQuery(id+"F9.wireOp",EDGE,"E3.1.2.6");Q5=makeQuery(id+"F9.imprint","IMPRINT",FACE,{"disambiguationData":[TD([[makeQuery(id+"F9.imprint","IMPRINT",EDGE,{"derivedFrom":subQ8}),1.0]])]});}
            var Q6;
            {var subQ4=sQuery(id+"F9.wireOp",EDGE,"E3.1.1.6");Q6=makeQuery(id+"F9.imprint","IMPRINT",FACE,{"disambiguationData":[TD([[makeQuery(id+"F9.imprint","IMPRINT",EDGE,{"derivedFrom":subQ4}),1.0]])]});}
            var Q7;
            {var subQ1=sQuery(id+"F9.wireOp",EDGE,"E3.1.0.6");Q7=makeQuery(id+"F9.imprint","IMPRINT",FACE,{"disambiguationData":[TD([[makeQuery(id+"F9.imprint","IMPRINT",EDGE,{"derivedFrom":subQ1}),1.0]])]});}
            var Q8;
            {var subQ8=sQuery(id+"F9.wireOp",EDGE,"E3.2.0.6");Q8=makeQuery(id+"F9.imprint","IMPRINT",FACE,{"disambiguationData":[TD([[makeQuery(id+"F9.imprint","IMPRINT",EDGE,{"derivedFrom":subQ8}),1.0]])]});}
            var Q9;
            {var subQ3=sQuery(id+"F9.wireOp",EDGE,"E3.2.1.6");Q9=makeQuery(id+"F9.imprint","IMPRINT",FACE,{"disambiguationData":[TD([[makeQuery(id+"F9.imprint","IMPRINT",EDGE,{"derivedFrom":subQ3}),1.0]])]});}
            var Q10;
            {var subQ3=sQuery(id+"F9.wireOp",EDGE,"E3.2.2.6");Q10=makeQuery(id+"F9.imprint","IMPRINT",FACE,{"disambiguationData":[TD([[makeQuery(id+"F9.imprint","IMPRINT",EDGE,{"derivedFrom":subQ3}),1.0]])]});}
            var Q11;
            {var subQ4=sQuery(id+"F9.wireOp",EDGE,"E3.2.3.5");Q11=makeQuery(id+"F9.imprint","IMPRINT",FACE,{"disambiguationData":[TD([[makeQuery(id+"F9.imprint","IMPRINT",EDGE,{"derivedFrom":subQ4}),-1.0]])]});}
            var Q12;
            {var subQ3=sQuery(id+"F17.wireOp",EDGE,"E7.1");Q12=makeQuery(id+"F17.imprint","IMPRINT",FACE,{"disambiguationData":[TD([[makeQuery(id+"F17.imprint","IMPRINT",EDGE,{"derivedFrom":subQ3}),1.0]])]});}
            var Q13;
            {var subQ1=sQuery(id+"F17.wireOp",EDGE,"E9.1.0.4");Q13=makeQuery(id+"F17.imprint","IMPRINT",FACE,{"disambiguationData":[TD([[makeQuery(id+"F17.imprint","IMPRINT",EDGE,{"derivedFrom":subQ1}),1.0]])]});}
            var Q14;
            {var subQ2=sQuery(id+"F17.wireOp",EDGE,"E9.2.0.4");Q14=makeQuery(id+"F17.imprint","IMPRINT",FACE,{"disambiguationData":[TD([[makeQuery(id+"F17.imprint","IMPRINT",EDGE,{"derivedFrom":subQ2}),1.0]])]});}
            var Q15;
            Q15=makeQuery(id+"F17.imprint","IMPRINT",FACE,{"disambiguationData":[TD([[makeQuery(id+"F17.imprint","IMPRINT",EDGE,{"derivedFrom":sQuery(id+"F17.wireOp",EDGE,"E9.2.1.2")}),1.0]])]});
            var Q16;
            {var subQ2=sQuery(id+"F17.wireOp",EDGE,"E9.1.1.2");Q16=makeQuery(id+"F17.imprint","IMPRINT",FACE,{"disambiguationData":[TD([[makeQuery(id+"F17.imprint","IMPRINT",EDGE,{"derivedFrom":subQ2}),1.0]])]});}
            var Q17;
            {var subQ1=sQuery(id+"F17.wireOp",EDGE,"E9.0.1.2");Q17=makeQuery(id+"F17.imprint","IMPRINT",FACE,{"disambiguationData":[TD([[makeQuery(id+"F17.imprint","IMPRINT",EDGE,{"derivedFrom":subQ1}),1.0]])]});}
            var Q18;
            Q18=makeQuery(id+"F6.opExtrude","SWEPT_FACE",FACE,{"disambiguationData":[OSD([sQuery(id+"F5.wireOp",EDGE,"E0.bottom")])]});
            extrude(context, id + "F20", {"entities" : qUnion([Q0, Q1, Q2, Q3, Q4, Q5, Q6, Q7, Q8, Q9, Q10, Q11, Q12, Q13, Q14, Q15, Q16, Q17]), "operationType" : NewBodyOperationType.REMOVE, "endBound" : BoundingType.UP_TO_SURFACE, "depth" : 25 * mm, "endBoundEntityFace" : qUnion([Q18]), "offsetDistance" : 25 * mm});
        }
        {
            var Q0;
            Q0=makeQuery(id+"F12.opExtrude","SWEPT_FACE",FACE,{"disambiguationData":[OSD([sQuery(id+"F11.wireOp",EDGE,"E4.bottom")])]});
            var sketch = newSketch(context, id + "F21", { "sketchPlane" : qUnion([Q0])});
            skLineSegment(sketch, "E11", {"start": v(-6.93, -11.3) * mm, "end": v(-6.93, -7.7) * mm});
            skLineSegment(sketch, "E12", {"start": v(-6.93, -7.7) * mm, "end": v(6.93, -7.7) * mm});
            skLineSegment(sketch, "E13", {"start": v(6.93, -7.7) * mm, "end": v(6.93, -11.3) * mm});
            skLineSegment(sketch, "E14", {"start": v(6.93, -11.3) * mm, "end": v(-6.93, -11.3) * mm});
            skLineSegment(sketch, "E15", {"start": v(14.87, -11.3) * mm, "end": v(14.87, -7.7) * mm});
            skLineSegment(sketch, "E16", {"start": v(14.87, -7.7) * mm, "end": v(28.73, -7.7) * mm});
            skLineSegment(sketch, "E17", {"start": v(28.73, -7.7) * mm, "end": v(28.73, -11.3) * mm});
            skLineSegment(sketch, "E18", {"start": v(28.73, -11.3) * mm, "end": v(14.87, -11.3) * mm});
            skLineSegment(sketch, "E19", {"start": v(36.67, -11.3) * mm, "end": v(36.67, -7.7) * mm});
            skLineSegment(sketch, "E20", {"start": v(36.67, -7.7) * mm, "end": v(50.53, -7.7) * mm});
            skLineSegment(sketch, "E21", {"start": v(50.53, -7.7) * mm, "end": v(50.53, -11.3) * mm});
            skLineSegment(sketch, "E22", {"start": v(50.53, -11.3) * mm, "end": v(36.67, -11.3) * mm});
            skSolve(sketch);
        }
        {
            var Q0;
            Q0=makeQuery(id+"F21.imprint","IMPRINT",FACE,{"disambiguationData":[TD([[makeQuery(id+"F21.imprint","IMPRINT",EDGE,{"derivedFrom":sQuery(id+"F21.wireOp",EDGE,"E11")}),-1.0]])]});
            var Q1;
            Q1=makeQuery(id+"F21.imprint","IMPRINT",FACE,{"disambiguationData":[TD([[makeQuery(id+"F21.imprint","IMPRINT",EDGE,{"derivedFrom":sQuery(id+"F21.wireOp",EDGE,"E15")}),-1.0]])]});
            var Q2;
            Q2=makeQuery(id+"F21.imprint","IMPRINT",FACE,{"disambiguationData":[TD([[makeQuery(id+"F21.imprint","IMPRINT",EDGE,{"derivedFrom":sQuery(id+"F21.wireOp",EDGE,"E19")}),-1.0]])]});
            var Q3;
            Q3=makeQuery(id+"F19.opExtrude","SWEPT_FACE",FACE,{"disambiguationData":[OSD([sQuery(id+"F18.wireOp",EDGE,"E10.bottom")])]});
            extrude(context, id + "F22", {"entities" : qUnion([Q0, Q1, Q2]), "operationType" : NewBodyOperationType.REMOVE, "endBound" : BoundingType.UP_TO_SURFACE, "oppositeDirection" : true, "depth" : 25 * mm, "endBoundEntityFace" : qUnion([Q3]), "offsetDistance" : 25 * mm});
        }
        {
            var Q0;
            {var subQ0=sQuery(id+"F21.wireOp",EDGE,"E11");var subQ1=sQuery(id+"F21.wireOp",EDGE,"E12");Q0=makeQuery(id+"F22.boolean.opBoolean","COPY",EDGE,{"disambiguationData":[TD([makeQuery(id+"F12.opExtrude","SWEPT_FACE",FACE,{"disambiguationData":[OSD([sQuery(id+"F11.wireOp",EDGE,"E4.bottom")])]})])],"derivedFrom":makeQuery(id+"F22.opExtrude","SWEPT_EDGE",EDGE,{"disambiguationData":[OSD([subQ0,subQ1])]})});}
            var Q1;
            {var subQ0=sQuery(id+"F21.wireOp",EDGE,"E12");var subQ1=sQuery(id+"F21.wireOp",EDGE,"E13");Q1=makeQuery(id+"F22.boolean.opBoolean","COPY",EDGE,{"disambiguationData":[TD([makeQuery(id+"F12.opExtrude","SWEPT_FACE",FACE,{"disambiguationData":[OSD([sQuery(id+"F11.wireOp",EDGE,"E4.bottom")])]})])],"derivedFrom":makeQuery(id+"F22.opExtrude","SWEPT_EDGE",EDGE,{"disambiguationData":[OSD([subQ0,subQ1])]})});}
            var Q2;
            {var subQ0=sQuery(id+"F21.wireOp",EDGE,"E16");var subQ1=sQuery(id+"F21.wireOp",EDGE,"E17");Q2=makeQuery(id+"F22.boolean.opBoolean","COPY",EDGE,{"disambiguationData":[TD([makeQuery(id+"F12.opExtrude","SWEPT_FACE",FACE,{"disambiguationData":[OSD([sQuery(id+"F11.wireOp",EDGE,"E4.bottom")])]})])],"derivedFrom":makeQuery(id+"F22.opExtrude","SWEPT_EDGE",EDGE,{"disambiguationData":[OSD([subQ0,subQ1])]})});}
            var Q3;
            {var subQ0=sQuery(id+"F21.wireOp",EDGE,"E15");var subQ1=sQuery(id+"F21.wireOp",EDGE,"E16");Q3=makeQuery(id+"F22.boolean.opBoolean","COPY",EDGE,{"disambiguationData":[TD([makeQuery(id+"F12.opExtrude","SWEPT_FACE",FACE,{"disambiguationData":[OSD([sQuery(id+"F11.wireOp",EDGE,"E4.bottom")])]})])],"derivedFrom":makeQuery(id+"F22.opExtrude","SWEPT_EDGE",EDGE,{"disambiguationData":[OSD([subQ0,subQ1])]})});}
            var Q4;
            {var subQ0=sQuery(id+"F21.wireOp",EDGE,"E19");var subQ1=sQuery(id+"F21.wireOp",EDGE,"E20");Q4=makeQuery(id+"F22.boolean.opBoolean","COPY",EDGE,{"disambiguationData":[TD([makeQuery(id+"F12.opExtrude","SWEPT_FACE",FACE,{"disambiguationData":[OSD([sQuery(id+"F11.wireOp",EDGE,"E4.bottom")])]})])],"derivedFrom":makeQuery(id+"F22.opExtrude","SWEPT_EDGE",EDGE,{"disambiguationData":[OSD([subQ0,subQ1])]})});}
            var Q5;
            {var subQ0=sQuery(id+"F21.wireOp",EDGE,"E20");var subQ1=sQuery(id+"F21.wireOp",EDGE,"E21");Q5=makeQuery(id+"F22.boolean.opBoolean","COPY",EDGE,{"disambiguationData":[TD([makeQuery(id+"F12.opExtrude","SWEPT_FACE",FACE,{"disambiguationData":[OSD([sQuery(id+"F11.wireOp",EDGE,"E4.bottom")])]})])],"derivedFrom":makeQuery(id+"F22.opExtrude","SWEPT_EDGE",EDGE,{"disambiguationData":[OSD([subQ0,subQ1])]})});}
            fillet(context, id + "F23", {"entities" : qUnion([Q0, Q1, Q2, Q3, Q4, Q5]), "radius" : 2.5 * mm, "tangentPropagation" : true, "allowEdgeOverflow" : false});
        }
        {
            var Q0;
            Q0=makeQuery(id+"F6.opExtrude","SWEPT_FACE",FACE,{"disambiguationData":[OSD([sQuery(id+"F5.wireOp",EDGE,"E0.top")])]});
            cPlane(context, id + "F24", {"entities" : qUnion([Q0]), "cplaneType" : CPlaneType.OFFSET, "offset" : (getVariable(context, 'WallThick')) * mm, "width" : 150 * mm, "height" : 150 * mm});
        }
        {
            var Q0;
            Q0=qCreatedBy(id+"F24.planeOp",FACE);
            var sketch = newSketch(context, id + "F25", { "sketchPlane" : qUnion([Q0])});
            skLineSegment(sketch, "E23.0", {"start": v(56.5, 50.8) * mm, "end": v(-12.9, 50.8) * mm});
            skLineSegment(sketch, "E23.1", {"start": v(56.5, 50.8) * mm, "end": v(56.5, -2.8) * mm});
            skLineSegment(sketch, "E23.2", {"start": v(56.5, -2.8) * mm, "end": v(-12.9, -2.8) * mm});
            skLineSegment(sketch, "E23.3", {"start": v(-12.9, 50.8) * mm, "end": v(-12.9, -2.8) * mm});
            skSolve(sketch);
        }
        {
            var Q0;
            Q0 = qSketchRegion(id + "F25", true);
            var Q1;
            Q1=makeQuery(id+"F19.boolean.opBoolean","MERGE",FACE,{"derivedFrom":[makeQuery(id+"F12.opExtrude","CAP_FACE",FACE,{"disambiguationData":[OSD([sQuery(id+"F11.wireOp",EDGE,"E4.bottom"),sQuery(id+"F11.wireOp",EDGE,"E4.top"),sQuery(id+"F11.wireOp",EDGE,"E4.left"),sQuery(id+"F11.wireOp",EDGE,"E4.right")])],"isStart":true}),makeQuery(id+"F19.opExtrude","CAP_FACE",FACE,{"disambiguationData":[OSD([sQuery(id+"F18.wireOp",EDGE,"E10.bottom"),sQuery(id+"F18.wireOp",EDGE,"E10.top"),sQuery(id+"F18.wireOp",EDGE,"E10.left"),sQuery(id+"F18.wireOp",EDGE,"E10.right")])],"isStart":true})]});
            extrude(context, id + "F26", {"entities" : qUnion([Q0]), "endBound" : BoundingType.UP_TO_SURFACE, "oppositeDirection" : true, "depth" : 25 * mm, "endBoundEntityFace" : qUnion([Q1]), "offsetDistance" : 25 * mm});
        }
        {
            var Q0;
            Q0=makeQuery(id+"F6.opExtrude","SWEPT_FACE",FACE,{"disambiguationData":[OSD([sQuery(id+"F5.wireOp",EDGE,"E0.top")])]});
            var sketch = newSketch(context, id + "F27", { "sketchPlane" : qUnion([Q0])});
            skLineSegment(sketch, "E24.0", {"start": v(-11.7, 49.6) * mm, "end": v(-11.7, -1.6) * mm});
            skLineSegment(sketch, "E24.1", {"start": v(55.3, 49.6) * mm, "end": v(-11.7, 49.6) * mm});
            skLineSegment(sketch, "E24.2", {"start": v(55.3, 49.6) * mm, "end": v(55.3, -1.6) * mm});
            skLineSegment(sketch, "E24.3", {"start": v(55.3, -1.6) * mm, "end": v(-11.7, -1.6) * mm});
            skSolve(sketch);
        }
        {
            var Q0;
            Q0 = qSketchRegion(id + "F27", true);
            var Q1;
            Q1=makeQuery(id+"F26.opExtrude","CAP_FACE",FACE,{"disambiguationData":[OSD([sQuery(id+"F25.wireOp",EDGE,"E23.0"),sQuery(id+"F25.wireOp",EDGE,"E23.1"),sQuery(id+"F25.wireOp",EDGE,"E23.2"),sQuery(id+"F25.wireOp",EDGE,"E23.3")])],"isStart":false});
            extrude(context, id + "F28", {"entities" : qUnion([Q0]), "operationType" : NewBodyOperationType.REMOVE, "endBound" : BoundingType.UP_TO_SURFACE, "oppositeDirection" : true, "depth" : 25 * mm, "endBoundEntityFace" : qUnion([Q1]), "offsetDistance" : 25 * mm});
        }
        {
            var Q0;
            Q0=makeQuery(id+"F28.boolean.opBoolean","COPY",FACE,{"derivedFrom":makeQuery(id+"F28.opExtrude","SWEPT_FACE",FACE,{"disambiguationData":[OSD([sQuery(id+"F27.wireOp",EDGE,"E24.3")])]})});
            var sketch = newSketch(context, id + "F29", { "sketchPlane" : qUnion([Q0])});
            skLineSegment(sketch, "E25.bottom", {"start": v(11.7, -11.3) * mm, "end": v(-55.3, -11.3) * mm});
            skLineSegment(sketch, "E25.top", {"start": v(11.7, -9.5) * mm, "end": v(-55.3, -9.5) * mm});
            skLineSegment(sketch, "E25.left", {"start": v(11.7, -11.3) * mm, "end": v(11.7, -9.5) * mm});
            skLineSegment(sketch, "E25.right", {"start": v(-55.3, -11.3) * mm, "end": v(-55.3, -9.5) * mm});
            skSolve(sketch);
        }
        {
            var Q0;
            Q0=makeQuery(id+"F28.boolean.opBoolean","COPY",FACE,{"derivedFrom":makeQuery(id+"F28.opExtrude","SWEPT_FACE",FACE,{"disambiguationData":[OSD([sQuery(id+"F27.wireOp",EDGE,"E24.0")])]})});
            var sketch = newSketch(context, id + "F30", { "sketchPlane" : qUnion([Q0])});
            skLineSegment(sketch, "E26.bottom", {"start": v(49.6, -11.3) * mm, "end": v(-1.6, -11.3) * mm});
            skLineSegment(sketch, "E26.top", {"start": v(49.6, -9.5) * mm, "end": v(-1.6, -9.5) * mm});
            skLineSegment(sketch, "E26.left", {"start": v(49.6, -11.3) * mm, "end": v(49.6, -9.5) * mm});
            skLineSegment(sketch, "E26.right", {"start": v(-1.6, -11.3) * mm, "end": v(-1.6, -9.5) * mm});
            skSolve(sketch);
        }
        {
            var Q0;
            Q0=makeQuery(id+"F28.boolean.opBoolean","COPY",FACE,{"derivedFrom":makeQuery(id+"F28.opExtrude","SWEPT_FACE",FACE,{"disambiguationData":[OSD([sQuery(id+"F27.wireOp",EDGE,"E24.2")])]})});
            var sketch = newSketch(context, id + "F31", { "sketchPlane" : qUnion([Q0])});
            skLineSegment(sketch, "E27.bottom", {"start": v(1.6, -11.3) * mm, "end": v(-49.6, -11.3) * mm});
            skLineSegment(sketch, "E27.top", {"start": v(1.6, -9.5) * mm, "end": v(-49.6, -9.5) * mm});
            skLineSegment(sketch, "E27.left", {"start": v(1.6, -11.3) * mm, "end": v(1.6, -9.5) * mm});
            skLineSegment(sketch, "E27.right", {"start": v(-49.6, -11.3) * mm, "end": v(-49.6, -9.5) * mm});
            skSolve(sketch);
        }
        {
            var Q0;
            Q0=makeQuery(id+"F28.boolean.opBoolean","COPY",FACE,{"derivedFrom":makeQuery(id+"F28.opExtrude","SWEPT_FACE",FACE,{"disambiguationData":[OSD([sQuery(id+"F27.wireOp",EDGE,"E24.1")])]})});
            var sketch = newSketch(context, id + "F32", { "sketchPlane" : qUnion([Q0])});
            skLineSegment(sketch, "E28.bottom", {"start": v(55.5, -11.3) * mm, "end": v(-11.5, -11.3) * mm});
            skLineSegment(sketch, "E28.top", {"start": v(55.5, -9.5) * mm, "end": v(-11.5, -9.5) * mm});
            skLineSegment(sketch, "E28.left", {"start": v(55.5, -11.3) * mm, "end": v(55.5, -9.5) * mm});
            skLineSegment(sketch, "E28.right", {"start": v(-11.5, -11.3) * mm, "end": v(-11.5, -9.5) * mm});
            skSolve(sketch);
        }
        {
            var Q0;
            Q0=makeQuery(id+"F29.imprint","IMPRINT",FACE,{"disambiguationData":[TD([[makeQuery(id+"F29.imprint","IMPRINT",EDGE,{"derivedFrom":sQuery(id+"F29.wireOp",EDGE,"E25.bottom")}),1.0]])]});
            extrude(context, id + "F33", {"entities" : qUnion([Q0]), "operationType" : NewBodyOperationType.ADD, "depth" : (getVariable(context, 'Offset')) * mm, "offsetDistance" : 25 * mm});
        }
        {
            var Q0;
            Q0=makeQuery(id+"F30.imprint","IMPRINT",FACE,{"disambiguationData":[TD([[makeQuery(id+"F30.imprint","IMPRINT",EDGE,{"derivedFrom":sQuery(id+"F30.wireOp",EDGE,"E26.bottom")}),-1.0]])]});
            extrude(context, id + "F34", {"entities" : qUnion([Q0]), "operationType" : NewBodyOperationType.ADD, "depth" : (getVariable(context, 'Offset')) * mm, "offsetDistance" : 25 * mm});
        }
        {
            var Q0;
            Q0 = qSketchRegion(id + "F31", true);
            extrude(context, id + "F35", {"entities" : qUnion([Q0]), "operationType" : NewBodyOperationType.ADD, "depth" : (getVariable(context, 'Offset')) * mm, "offsetDistance" : 25 * mm});
        }
        {
            var Q0;
            Q0 = qSketchRegion(id + "F32", true);
            extrude(context, id + "F36", {"entities" : qUnion([Q0]), "operationType" : NewBodyOperationType.ADD, "depth" : (getVariable(context, 'Offset')) * mm, "offsetDistance" : 25 * mm});
        }
        {
            var Q0;
            Q0=makeQuery(id+"F33.opExtrude","CAP_EDGE",EDGE,{"disambiguationData":[OSD([sQuery(id+"F29.wireOp",EDGE,"E25.bottom")])],"isStart":false});
            var Q1;
            Q1=makeQuery(id+"F33.opExtrude","CAP_EDGE",EDGE,{"disambiguationData":[OSD([sQuery(id+"F29.wireOp",EDGE,"E25.top")])],"isStart":false});
            var Q2;
            Q2=makeQuery(id+"F34.opExtrude","CAP_EDGE",EDGE,{"disambiguationData":[OSD([sQuery(id+"F30.wireOp",EDGE,"E26.bottom")])],"isStart":false});
            var Q3;
            Q3=makeQuery(id+"F34.opExtrude","CAP_EDGE",EDGE,{"disambiguationData":[OSD([sQuery(id+"F30.wireOp",EDGE,"E26.top")])],"isStart":false});
            var Q4;
            Q4=makeQuery(id+"F35.opExtrude","CAP_EDGE",EDGE,{"disambiguationData":[OSD([sQuery(id+"F31.wireOp",EDGE,"E27.bottom")])],"isStart":false});
            var Q5;
            Q5=makeQuery(id+"F35.opExtrude","CAP_EDGE",EDGE,{"disambiguationData":[OSD([sQuery(id+"F31.wireOp",EDGE,"E27.top")])],"isStart":false});
            var Q6;
            Q6=makeQuery(id+"F36.opExtrude","CAP_EDGE",EDGE,{"disambiguationData":[OSD([sQuery(id+"F32.wireOp",EDGE,"E28.bottom")])],"isStart":false});
            var Q7;
            Q7=makeQuery(id+"F36.opExtrude","CAP_EDGE",EDGE,{"disambiguationData":[OSD([sQuery(id+"F32.wireOp",EDGE,"E28.top")])],"isStart":false});
            chamfer(context, id + "F37", {"entities" : qUnion([Q0, Q1, Q2, Q3, Q4, Q5, Q6, Q7]), "width" : (getVariable(context, 'Offset')) * mm, "tangentPropagation" : true});
        }
        {
            var Q0;
            Q0=makeQuery(id+"F26.opExtrude","SWEPT_FACE",FACE,{"disambiguationData":[OSD([sQuery(id+"F25.wireOp",EDGE,"E23.2")])]});
            var sketch = newSketch(context, id + "F38", { "sketchPlane" : qUnion([Q0])});
            skLineSegment(sketch, "E29", {"start": v(21.8, -14.9) * mm, "end": v(21.8, 15.72) * mm, "construction": true});
            skPoint(sketch, "E29.startSnap0", {"position": v(21.8, -11.3) * mm});
            skPoint(sketch, "E29.endSnap0", {"position": v(21.8, 11.3) * mm});
            skLineSegment(sketch, "E30", {"start": v(2.17, -11.3) * mm, "end": v(2.17, 1.06) * mm});
            skLineSegment(sketch, "E31", {"start": v(41.43, 1.06) * mm, "end": v(41.43, -11.3) * mm});
            skLineSegment(sketch, "E32", {"start": v(2.17, 1.06) * mm, "end": v(41.43, 1.06) * mm});
            skSolve(sketch);
        }
        {
            var Q0;
            {var subQ0=sQuery(id+"F38.wireOp",EDGE,"E30");Q0=makeQuery(id+"F38.imprint","IMPRINT",FACE,{"disambiguationData":[TD([[makeQuery(id+"F38.imprint","IMPRINT",EDGE,{"derivedFrom":subQ0}),-1.0]])]});}
            var Q1;
            Q1=makeQuery(id+"F26.opExtrude","SWEPT_FACE",FACE,{"disambiguationData":[OSD([sQuery(id+"F25.wireOp",EDGE,"E23.0")])]});
            extrude(context, id + "F39", {"entities" : qUnion([Q0]), "operationType" : NewBodyOperationType.REMOVE, "endBound" : BoundingType.UP_TO_SURFACE, "oppositeDirection" : true, "depth" : 25 * mm, "endBoundEntityFace" : qUnion([Q1]), "offsetDistance" : 25 * mm});
        }
        {
            var Q0;
            Q0=makeQuery(id+"F26.opExtrude","SWEPT_FACE",FACE,{"disambiguationData":[OSD([sQuery(id+"F25.wireOp",EDGE,"E23.3")])]});
            var sketch = newSketch(context, id + "F40", { "sketchPlane" : qUnion([Q0])});
            skLineSegment(sketch, "E33", {"start": v(-40.9, -11.3) * mm, "end": v(-40.9, 1.06) * mm});
            skLineSegment(sketch, "E34", {"start": v(-40.9, 1.06) * mm, "end": v(-7.1, 1.06) * mm});
            skLineSegment(sketch, "E35", {"start": v(-7.1, 1.06) * mm, "end": v(-7.1, -11.3) * mm});
            skLineSegment(sketch, "E36", {"start": v(-24, -14.34) * mm, "end": v(-24, 14.16) * mm, "construction": true});
            skSolve(sketch);
        }
        {
            var Q0;
            {var subQ0=sQuery(id+"F40.wireOp",EDGE,"E33");Q0=makeQuery(id+"F40.imprint","IMPRINT",FACE,{"disambiguationData":[TD([[makeQuery(id+"F40.imprint","IMPRINT",EDGE,{"derivedFrom":subQ0}),-1.0]])]});}
            var Q1;
            Q1=makeQuery(id+"F26.opExtrude","SWEPT_FACE",FACE,{"disambiguationData":[OSD([sQuery(id+"F25.wireOp",EDGE,"E23.1")])]});
            extrude(context, id + "F41", {"entities" : qUnion([Q0]), "operationType" : NewBodyOperationType.REMOVE, "endBound" : BoundingType.UP_TO_SURFACE, "oppositeDirection" : true, "depth" : 25 * mm, "endBoundEntityFace" : qUnion([Q1]), "offsetDistance" : 25 * mm});
        }
        {
            var Q0;
            {var subQ0=sQuery(id+"F38.wireOp",EDGE,"E30");var subQ1=sQuery(id+"F38.wireOp",EDGE,"E32");Q0=makeQuery(id+"F39.boolean.opBoolean","COPY",EDGE,{"disambiguationData":[TD([makeQuery(id+"F26.opExtrude","SWEPT_FACE",FACE,{"disambiguationData":[OSD([sQuery(id+"F25.wireOp",EDGE,"E23.2")])]})])],"derivedFrom":makeQuery(id+"F39.opExtrude","SWEPT_EDGE",EDGE,{"disambiguationData":[OSD([subQ0,subQ1])]})});}
            var Q1;
            {var subQ0=sQuery(id+"F38.wireOp",EDGE,"E31");var subQ1=sQuery(id+"F38.wireOp",EDGE,"E32");Q1=makeQuery(id+"F39.boolean.opBoolean","COPY",EDGE,{"disambiguationData":[TD([makeQuery(id+"F26.opExtrude","SWEPT_FACE",FACE,{"disambiguationData":[OSD([sQuery(id+"F25.wireOp",EDGE,"E23.2")])]})])],"derivedFrom":makeQuery(id+"F39.opExtrude","SWEPT_EDGE",EDGE,{"disambiguationData":[OSD([subQ0,subQ1])]})});}
            var Q2;
            {var subQ0=sQuery(id+"F38.wireOp",EDGE,"E32");var subQ1=sQuery(id+"F38.wireOp",EDGE,"E30");Q2=makeQuery(id+"F39.boolean.opBoolean","COPY",EDGE,{"disambiguationData":[TD([makeQuery(id+"F26.opExtrude","SWEPT_FACE",FACE,{"disambiguationData":[OSD([sQuery(id+"F25.wireOp",EDGE,"E23.0")])]})])],"derivedFrom":makeQuery(id+"F39.opExtrude","SWEPT_EDGE",EDGE,{"disambiguationData":[OSD([subQ1,subQ0])]})});}
            var Q3;
            {var subQ0=sQuery(id+"F38.wireOp",EDGE,"E32");var subQ1=sQuery(id+"F38.wireOp",EDGE,"E31");Q3=makeQuery(id+"F39.boolean.opBoolean","COPY",EDGE,{"disambiguationData":[TD([makeQuery(id+"F26.opExtrude","SWEPT_FACE",FACE,{"disambiguationData":[OSD([sQuery(id+"F25.wireOp",EDGE,"E23.0")])]})])],"derivedFrom":makeQuery(id+"F39.opExtrude","SWEPT_EDGE",EDGE,{"disambiguationData":[OSD([subQ1,subQ0])]})});}
            var Q4;
            {var subQ0=sQuery(id+"F40.wireOp",EDGE,"E34");var subQ1=sQuery(id+"F40.wireOp",EDGE,"E33");Q4=makeQuery(id+"F41.boolean.opBoolean","COPY",EDGE,{"disambiguationData":[TD([makeQuery(id+"F26.opExtrude","SWEPT_FACE",FACE,{"disambiguationData":[OSD([sQuery(id+"F25.wireOp",EDGE,"E23.3")])]})])],"derivedFrom":makeQuery(id+"F41.opExtrude","SWEPT_EDGE",EDGE,{"disambiguationData":[OSD([subQ1,subQ0])]})});}
            var Q5;
            {var subQ0=sQuery(id+"F40.wireOp",EDGE,"E35");var subQ1=sQuery(id+"F40.wireOp",EDGE,"E34");Q5=makeQuery(id+"F41.boolean.opBoolean","COPY",EDGE,{"disambiguationData":[TD([makeQuery(id+"F26.opExtrude","SWEPT_FACE",FACE,{"disambiguationData":[OSD([sQuery(id+"F25.wireOp",EDGE,"E23.3")])]})])],"derivedFrom":makeQuery(id+"F41.opExtrude","SWEPT_EDGE",EDGE,{"disambiguationData":[OSD([subQ1,subQ0])]})});}
            var Q6;
            {var subQ0=sQuery(id+"F40.wireOp",EDGE,"E34");var subQ1=sQuery(id+"F40.wireOp",EDGE,"E35");Q6=makeQuery(id+"F41.boolean.opBoolean","COPY",EDGE,{"disambiguationData":[TD([makeQuery(id+"F26.opExtrude","SWEPT_FACE",FACE,{"disambiguationData":[OSD([sQuery(id+"F25.wireOp",EDGE,"E23.1")])]})])],"derivedFrom":makeQuery(id+"F41.opExtrude","SWEPT_EDGE",EDGE,{"disambiguationData":[OSD([subQ0,subQ1])]})});}
            var Q7;
            {var subQ0=sQuery(id+"F40.wireOp",EDGE,"E33");var subQ1=sQuery(id+"F40.wireOp",EDGE,"E34");Q7=makeQuery(id+"F41.boolean.opBoolean","COPY",EDGE,{"disambiguationData":[TD([makeQuery(id+"F26.opExtrude","SWEPT_FACE",FACE,{"disambiguationData":[OSD([sQuery(id+"F25.wireOp",EDGE,"E23.1")])]})])],"derivedFrom":makeQuery(id+"F41.opExtrude","SWEPT_EDGE",EDGE,{"disambiguationData":[OSD([subQ0,subQ1])]})});}
            fillet(context, id + "F42", {"entities" : qUnion([Q0, Q1, Q2, Q3, Q4, Q5, Q6, Q7]), "radius" : 5 * mm, "tangentPropagation" : true, "allowEdgeOverflow" : false});
        }
        {
            var Q0;
            {var subQ0=sQuery(id+"F18.wireOp",EDGE,"E10.right");var subQ1=sQuery(id+"F18.wireOp",EDGE,"E10.left");var subQ2=sQuery(id+"F18.wireOp",EDGE,"E10.top");var subQ3=sQuery(id+"F18.wireOp",EDGE,"E10.bottom");var subQ4=sQuery(id+"F11.wireOp",EDGE,"E4.right");var subQ5=sQuery(id+"F11.wireOp",EDGE,"E4.left");var subQ6=sQuery(id+"F11.wireOp",EDGE,"E4.top");var subQ7=sQuery(id+"F11.wireOp",EDGE,"E4.bottom");var subQ8=sQuery(id+"F38.wireOp",EDGE,"E31");var subQ9=sQuery(id+"F25.wireOp",EDGE,"E23.2");Q0=makeQuery(id+"F39.boolean.opBoolean","COPY",EDGE,{"disambiguationData":[TD([makeQuery(id+"F26.opExtrude","SWEPT_FACE",FACE,{"disambiguationData":[OSD([subQ9])]})])],"derivedFrom":makeQuery(id+"F39.opExtrude","SWEPT_EDGE",EDGE,{"disambiguationData":[OSD([subQ7,subQ6,subQ5,subQ4,subQ3,subQ2,subQ1,subQ0,subQ9,subQ8])]})});}
            var Q1;
            {var subQ0=sQuery(id+"F18.wireOp",EDGE,"E10.right");var subQ1=sQuery(id+"F18.wireOp",EDGE,"E10.left");var subQ2=sQuery(id+"F18.wireOp",EDGE,"E10.top");var subQ3=sQuery(id+"F18.wireOp",EDGE,"E10.bottom");var subQ4=sQuery(id+"F11.wireOp",EDGE,"E4.right");var subQ5=sQuery(id+"F11.wireOp",EDGE,"E4.left");var subQ6=sQuery(id+"F11.wireOp",EDGE,"E4.top");var subQ7=sQuery(id+"F11.wireOp",EDGE,"E4.bottom");var subQ8=sQuery(id+"F40.wireOp",EDGE,"E35");Q1=makeQuery(id+"F41.boolean.opBoolean","COPY",EDGE,{"disambiguationData":[TD([makeQuery(id+"F26.opExtrude","SWEPT_FACE",FACE,{"disambiguationData":[OSD([sQuery(id+"F25.wireOp",EDGE,"E23.1")])]})])],"derivedFrom":makeQuery(id+"F41.opExtrude","SWEPT_EDGE",EDGE,{"disambiguationData":[OSD([subQ7,subQ6,subQ5,subQ4,subQ3,subQ2,subQ1,subQ0,sQuery(id+"F25.wireOp",EDGE,"E23.3"),subQ8])]})});}
            var Q2;
            {var subQ0=sQuery(id+"F18.wireOp",EDGE,"E10.right");var subQ1=sQuery(id+"F18.wireOp",EDGE,"E10.left");var subQ2=sQuery(id+"F18.wireOp",EDGE,"E10.top");var subQ3=sQuery(id+"F18.wireOp",EDGE,"E10.bottom");var subQ4=sQuery(id+"F11.wireOp",EDGE,"E4.right");var subQ5=sQuery(id+"F11.wireOp",EDGE,"E4.left");var subQ6=sQuery(id+"F11.wireOp",EDGE,"E4.top");var subQ7=sQuery(id+"F11.wireOp",EDGE,"E4.bottom");var subQ8=sQuery(id+"F40.wireOp",EDGE,"E33");Q2=makeQuery(id+"F41.boolean.opBoolean","COPY",EDGE,{"disambiguationData":[TD([makeQuery(id+"F26.opExtrude","SWEPT_FACE",FACE,{"disambiguationData":[OSD([sQuery(id+"F25.wireOp",EDGE,"E23.1")])]})])],"derivedFrom":makeQuery(id+"F41.opExtrude","SWEPT_EDGE",EDGE,{"disambiguationData":[OSD([subQ7,subQ6,subQ5,subQ4,subQ3,subQ2,subQ1,subQ0,sQuery(id+"F25.wireOp",EDGE,"E23.3"),subQ8])]})});}
            var Q3;
            {var subQ0=sQuery(id+"F18.wireOp",EDGE,"E10.right");var subQ1=sQuery(id+"F18.wireOp",EDGE,"E10.left");var subQ2=sQuery(id+"F18.wireOp",EDGE,"E10.top");var subQ3=sQuery(id+"F18.wireOp",EDGE,"E10.bottom");var subQ4=sQuery(id+"F11.wireOp",EDGE,"E4.right");var subQ5=sQuery(id+"F11.wireOp",EDGE,"E4.left");var subQ6=sQuery(id+"F11.wireOp",EDGE,"E4.top");var subQ7=sQuery(id+"F11.wireOp",EDGE,"E4.bottom");var subQ8=sQuery(id+"F38.wireOp",EDGE,"E31");Q3=makeQuery(id+"F39.boolean.opBoolean","COPY",EDGE,{"disambiguationData":[TD([makeQuery(id+"F26.opExtrude","SWEPT_FACE",FACE,{"disambiguationData":[OSD([sQuery(id+"F25.wireOp",EDGE,"E23.0")])]})])],"derivedFrom":makeQuery(id+"F39.opExtrude","SWEPT_EDGE",EDGE,{"disambiguationData":[OSD([subQ7,subQ6,subQ5,subQ4,subQ3,subQ2,subQ1,subQ0,sQuery(id+"F25.wireOp",EDGE,"E23.2"),subQ8])]})});}
            var Q4;
            {var subQ0=sQuery(id+"F18.wireOp",EDGE,"E10.right");var subQ1=sQuery(id+"F18.wireOp",EDGE,"E10.left");var subQ2=sQuery(id+"F18.wireOp",EDGE,"E10.top");var subQ3=sQuery(id+"F18.wireOp",EDGE,"E10.bottom");var subQ4=sQuery(id+"F11.wireOp",EDGE,"E4.right");var subQ5=sQuery(id+"F11.wireOp",EDGE,"E4.left");var subQ6=sQuery(id+"F11.wireOp",EDGE,"E4.top");var subQ7=sQuery(id+"F11.wireOp",EDGE,"E4.bottom");var subQ8=sQuery(id+"F38.wireOp",EDGE,"E30");Q4=makeQuery(id+"F39.boolean.opBoolean","COPY",EDGE,{"disambiguationData":[TD([makeQuery(id+"F26.opExtrude","SWEPT_FACE",FACE,{"disambiguationData":[OSD([sQuery(id+"F25.wireOp",EDGE,"E23.0")])]})])],"derivedFrom":makeQuery(id+"F39.opExtrude","SWEPT_EDGE",EDGE,{"disambiguationData":[OSD([subQ7,subQ6,subQ5,subQ4,subQ3,subQ2,subQ1,subQ0,sQuery(id+"F25.wireOp",EDGE,"E23.2"),subQ8])]})});}
            var Q5;
            {var subQ0=sQuery(id+"F18.wireOp",EDGE,"E10.right");var subQ1=sQuery(id+"F18.wireOp",EDGE,"E10.left");var subQ2=sQuery(id+"F18.wireOp",EDGE,"E10.top");var subQ3=sQuery(id+"F18.wireOp",EDGE,"E10.bottom");var subQ4=sQuery(id+"F11.wireOp",EDGE,"E4.right");var subQ5=sQuery(id+"F11.wireOp",EDGE,"E4.left");var subQ6=sQuery(id+"F11.wireOp",EDGE,"E4.top");var subQ7=sQuery(id+"F11.wireOp",EDGE,"E4.bottom");var subQ8=sQuery(id+"F25.wireOp",EDGE,"E23.3");var subQ9=sQuery(id+"F40.wireOp",EDGE,"E33");Q5=makeQuery(id+"F41.boolean.opBoolean","COPY",EDGE,{"disambiguationData":[TD([makeQuery(id+"F26.opExtrude","SWEPT_FACE",FACE,{"disambiguationData":[OSD([subQ8])]})])],"derivedFrom":makeQuery(id+"F41.opExtrude","SWEPT_EDGE",EDGE,{"disambiguationData":[OSD([subQ7,subQ6,subQ5,subQ4,subQ3,subQ2,subQ1,subQ0,subQ8,subQ9])]})});}
            var Q6;
            {var subQ0=sQuery(id+"F18.wireOp",EDGE,"E10.right");var subQ1=sQuery(id+"F18.wireOp",EDGE,"E10.left");var subQ2=sQuery(id+"F18.wireOp",EDGE,"E10.top");var subQ3=sQuery(id+"F18.wireOp",EDGE,"E10.bottom");var subQ4=sQuery(id+"F11.wireOp",EDGE,"E4.right");var subQ5=sQuery(id+"F11.wireOp",EDGE,"E4.left");var subQ6=sQuery(id+"F11.wireOp",EDGE,"E4.top");var subQ7=sQuery(id+"F11.wireOp",EDGE,"E4.bottom");var subQ8=sQuery(id+"F25.wireOp",EDGE,"E23.3");var subQ9=sQuery(id+"F40.wireOp",EDGE,"E35");Q6=makeQuery(id+"F41.boolean.opBoolean","COPY",EDGE,{"disambiguationData":[TD([makeQuery(id+"F26.opExtrude","SWEPT_FACE",FACE,{"disambiguationData":[OSD([subQ8])]})])],"derivedFrom":makeQuery(id+"F41.opExtrude","SWEPT_EDGE",EDGE,{"disambiguationData":[OSD([subQ7,subQ6,subQ5,subQ4,subQ3,subQ2,subQ1,subQ0,subQ8,subQ9])]})});}
            var Q7;
            {var subQ0=sQuery(id+"F18.wireOp",EDGE,"E10.right");var subQ1=sQuery(id+"F18.wireOp",EDGE,"E10.left");var subQ2=sQuery(id+"F18.wireOp",EDGE,"E10.top");var subQ3=sQuery(id+"F18.wireOp",EDGE,"E10.bottom");var subQ4=sQuery(id+"F11.wireOp",EDGE,"E4.right");var subQ5=sQuery(id+"F11.wireOp",EDGE,"E4.left");var subQ6=sQuery(id+"F11.wireOp",EDGE,"E4.top");var subQ7=sQuery(id+"F11.wireOp",EDGE,"E4.bottom");var subQ8=sQuery(id+"F25.wireOp",EDGE,"E23.2");var subQ9=sQuery(id+"F38.wireOp",EDGE,"E30");Q7=makeQuery(id+"F39.boolean.opBoolean","COPY",EDGE,{"disambiguationData":[TD([makeQuery(id+"F26.opExtrude","SWEPT_FACE",FACE,{"disambiguationData":[OSD([subQ8])]})])],"derivedFrom":makeQuery(id+"F39.opExtrude","SWEPT_EDGE",EDGE,{"disambiguationData":[OSD([subQ7,subQ6,subQ5,subQ4,subQ3,subQ2,subQ1,subQ0,subQ8,subQ9])]})});}
            fillet(context, id + "F43", {"entities" : qUnion([Q0, Q1, Q2, Q3, Q4, Q5, Q6, Q7]), "radius" : 5 * mm, "tangentPropagation" : true, "allowEdgeOverflow" : false});
        }
        {
            var Q0;
            Q0=makeQuery(id+"F26.opExtrude","CAP_FACE",FACE,{"disambiguationData":[OSD([sQuery(id+"F25.wireOp",EDGE,"E23.0"),sQuery(id+"F25.wireOp",EDGE,"E23.1"),sQuery(id+"F25.wireOp",EDGE,"E23.2"),sQuery(id+"F25.wireOp",EDGE,"E23.3")])],"isStart":true});
            var sketch = newSketch(context, id + "F44", { "sketchPlane" : qUnion([Q0])});
            skText(sketch, "E37", { "text": "Tales", "fontName": "NotoSerif-Regular.ttf"});
            skText(sketch, "E38", { "text": "Arabian Nights", "fontName": "NotoSerif-Regular.ttf"});
            skText(sketch, "E39", { "text": "of the", "fontName": "NotoSerif-Regular.ttf"});
            const initialGuessF44  = {"E37": [0.00246, 0.03549, 1, 0, 0.01118], "E38": [-0.0111, 0.008, 1, 0, 0.00657], "E39": [0.00829, 0.0235, 1, 0, 0.0071]};
            skSetInitialGuess(sketch, initialGuessF44);
            skSolve(sketch);
        }
        {
            var Q0;
            Q0 = qSketchRegion(id + "F44", true);
            extrude(context, id + "F45", {"entities" : qUnion([Q0]), "operationType" : NewBodyOperationType.REMOVE, "oppositeDirection" : true, "depth" : (getVariable(context, 'WallThick') / 2) * mm, "offsetDistance" : 25 * mm});
        }
    });